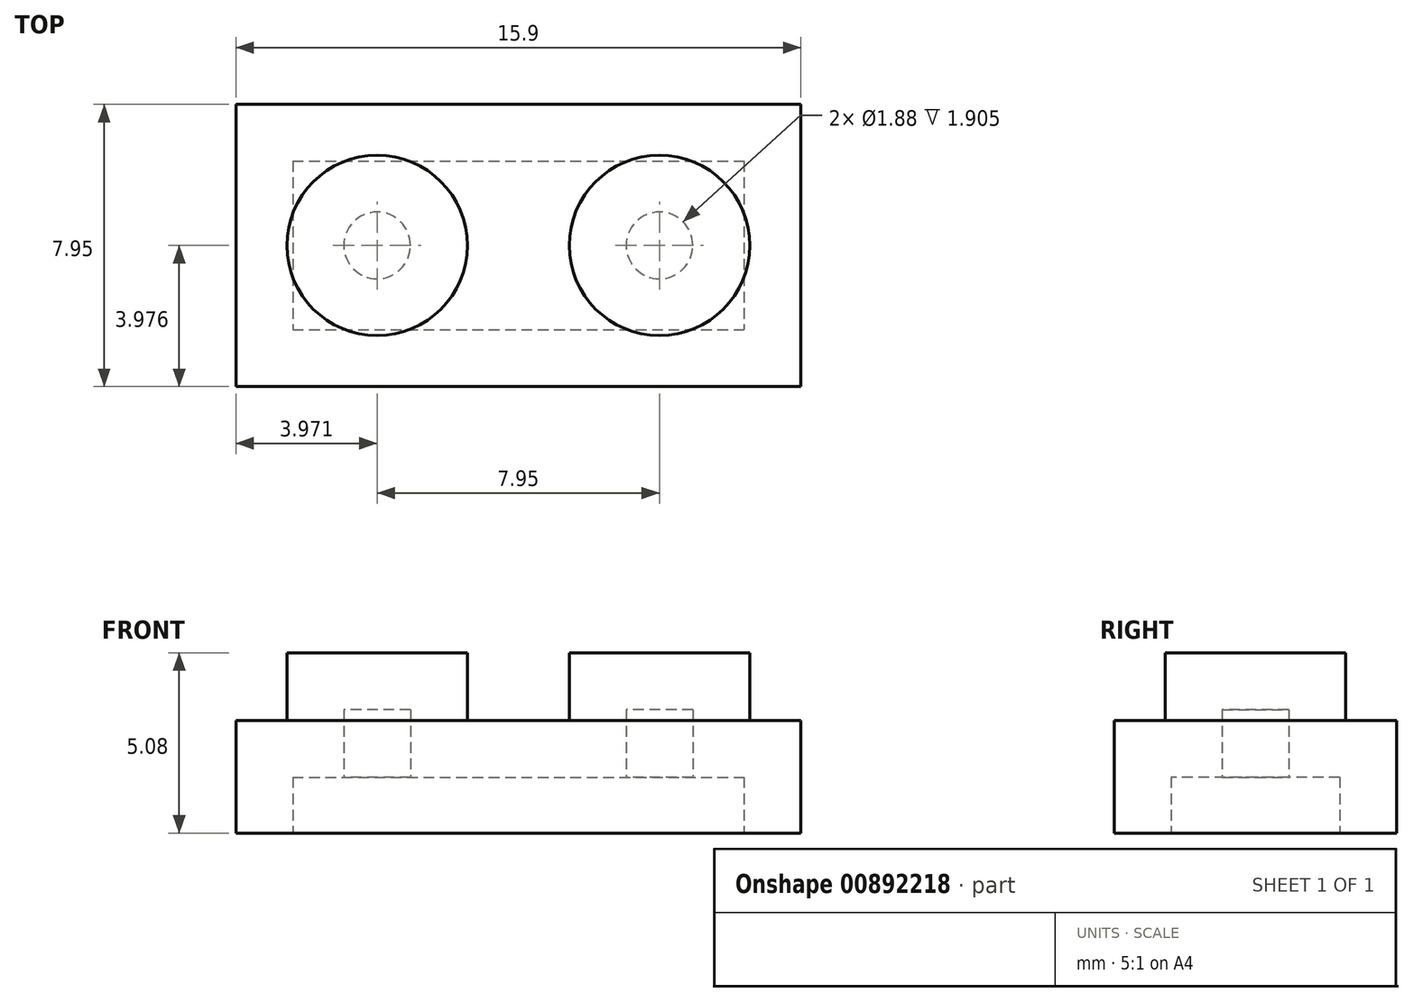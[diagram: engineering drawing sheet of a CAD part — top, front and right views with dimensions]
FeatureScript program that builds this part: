
annotation { "Feature Type Name" : "Feature", "Feature Type Description" : "" }
export const myFeature = defineFeature(function(context is Context, id is Id, definition is map)
    precondition{}
    {
        {
            var Q0;
            Q0=qCreatedBy(makeId("Top.planeOp"),FACE);
            var sketch = newSketch(context, id + "F0", { "sketchPlane" : qUnion([Q0])});
            skLineSegment(sketch, "E0.bottom", {"start": v(-57.35, -17.93) * mm, "end": v(-41.45, -17.93) * mm});
            skLineSegment(sketch, "E0.top", {"start": v(-57.35, -25.88) * mm, "end": v(-41.45, -25.88) * mm});
            skLineSegment(sketch, "E0.left", {"start": v(-57.35, -17.93) * mm, "end": v(-57.35, -25.88) * mm});
            skLineSegment(sketch, "E0.right", {"start": v(-41.45, -17.93) * mm, "end": v(-41.45, -25.88) * mm});
            skLineSegment(sketch, "E1", {"start": v(-53.38, -17.93) * mm, "end": v(-53.38, -25.88) * mm});
            skLineSegment(sketch, "E2", {"start": v(-45.43, -17.93) * mm, "end": v(-45.43, -25.88) * mm});
            skCircle(sketch, "E3", {"center": v(-53.38, -21.9) * mm, "radius": 2.54 * mm});
            skCircle(sketch, "E4", {"center": v(-45.43, -21.9) * mm, "radius": 2.54 * mm});
            skSolve(sketch);
        }
        {
            var Q0;
            {var subQ0=sQuery(id+"F0.wireOp",EDGE,"E0.left");Q0=makeQuery(id+"F0.imprint","IMPRINT",FACE,{"disambiguationData":[TD([[makeQuery(id+"F0.imprint","IMPRINT",EDGE,{"derivedFrom":subQ0}),1.0]])]});}
            var Q1;
            {var subQ0=sQuery(id+"F0.wireOp",EDGE,"E1");var subQ5=sQuery(id+"F0.wireOp",EDGE,"E0.bottom");var subQ6=makeQuery(id+"F0.imprint","INTERSECT",VERTEX,{"derivedFrom":[subQ5,subQ0]});Q1=makeQuery(id+"F0.imprint","IMPRINT",FACE,{"disambiguationData":[TD([[makeQuery(id+"F0.imprint","IMPRINT",EDGE,{"disambiguationData":[TD([[subQ6,-1.0]])],"derivedFrom":subQ5}),-1.0]])]});}
            var Q2;
            {var subQ5=sQuery(id+"F0.wireOp",EDGE,"E0.right");Q2=makeQuery(id+"F0.imprint","IMPRINT",FACE,{"disambiguationData":[TD([[makeQuery(id+"F0.imprint","IMPRINT",EDGE,{"derivedFrom":subQ5}),-1.0]])]});}
            var Q3;
            {var subQ0=sQuery(id+"F0.wireOp",EDGE,"E4");var subQ1=sQuery(id+"F0.wireOp",EDGE,"E2");var subQ2=makeQuery(id+"F0.imprint","INTERSECT",VERTEX,{"disambiguationData":[OD(0.0)],"derivedFrom":[subQ1,subQ0]});Q3=makeQuery(id+"F0.imprint","IMPRINT",FACE,{"disambiguationData":[TD([[makeQuery(id+"F0.imprint","IMPRINT",EDGE,{"disambiguationData":[TD([[subQ2,-1.0]])],"derivedFrom":subQ1}),-1.0]])]});}
            var Q4;
            {var subQ0=sQuery(id+"F0.wireOp",EDGE,"E4");var subQ1=sQuery(id+"F0.wireOp",EDGE,"E2");var subQ2=makeQuery(id+"F0.imprint","INTERSECT",VERTEX,{"disambiguationData":[OD(0.0)],"derivedFrom":[subQ1,subQ0]});Q4=makeQuery(id+"F0.imprint","IMPRINT",FACE,{"disambiguationData":[TD([[makeQuery(id+"F0.imprint","IMPRINT",EDGE,{"disambiguationData":[TD([[subQ2,-1.0]])],"derivedFrom":subQ1}),1.0]])]});}
            var Q5;
            {var subQ0=sQuery(id+"F0.wireOp",EDGE,"E3");var subQ1=sQuery(id+"F0.wireOp",EDGE,"E1");var subQ2=makeQuery(id+"F0.imprint","INTERSECT",VERTEX,{"disambiguationData":[OD(0.0)],"derivedFrom":[subQ1,subQ0]});Q5=makeQuery(id+"F0.imprint","IMPRINT",FACE,{"disambiguationData":[TD([[makeQuery(id+"F0.imprint","IMPRINT",EDGE,{"disambiguationData":[TD([[subQ2,-1.0]])],"derivedFrom":subQ1}),1.0]])]});}
            var Q6;
            {var subQ0=sQuery(id+"F0.wireOp",EDGE,"E3");var subQ1=sQuery(id+"F0.wireOp",EDGE,"E1");var subQ2=makeQuery(id+"F0.imprint","INTERSECT",VERTEX,{"disambiguationData":[OD(0.0)],"derivedFrom":[subQ1,subQ0]});Q6=makeQuery(id+"F0.imprint","IMPRINT",FACE,{"disambiguationData":[TD([[makeQuery(id+"F0.imprint","IMPRINT",EDGE,{"disambiguationData":[TD([[subQ2,-1.0]])],"derivedFrom":subQ1}),-1.0]])]});}
            extrude(context, id + "F1", {"entities" : qUnion([Q0, Q1, Q2, Q3, Q4, Q5, Q6]), "depth" : 3.17 * mm, "offsetDistance" : 25.4 * mm});
        }
        {
            var Q0;
            {var subQ0=sQuery(id+"F0.wireOp",EDGE,"E3");var subQ1=sQuery(id+"F0.wireOp",EDGE,"E1");var subQ2=makeQuery(id+"F0.imprint","INTERSECT",VERTEX,{"disambiguationData":[OD(0.0)],"derivedFrom":[subQ1,subQ0]});Q0=makeQuery(id+"F0.imprint","IMPRINT",FACE,{"disambiguationData":[TD([[makeQuery(id+"F0.imprint","IMPRINT",EDGE,{"disambiguationData":[TD([[subQ2,-1.0]])],"derivedFrom":subQ1}),-1.0]])]});}
            var Q1;
            {var subQ0=sQuery(id+"F0.wireOp",EDGE,"E3");var subQ1=sQuery(id+"F0.wireOp",EDGE,"E1");var subQ2=makeQuery(id+"F0.imprint","INTERSECT",VERTEX,{"disambiguationData":[OD(0.0)],"derivedFrom":[subQ1,subQ0]});Q1=makeQuery(id+"F0.imprint","IMPRINT",FACE,{"disambiguationData":[TD([[makeQuery(id+"F0.imprint","IMPRINT",EDGE,{"disambiguationData":[TD([[subQ2,-1.0]])],"derivedFrom":subQ1}),1.0]])]});}
            var Q2;
            {var subQ0=sQuery(id+"F0.wireOp",EDGE,"E4");var subQ1=sQuery(id+"F0.wireOp",EDGE,"E2");var subQ2=makeQuery(id+"F0.imprint","INTERSECT",VERTEX,{"disambiguationData":[OD(0.0)],"derivedFrom":[subQ1,subQ0]});Q2=makeQuery(id+"F0.imprint","IMPRINT",FACE,{"disambiguationData":[TD([[makeQuery(id+"F0.imprint","IMPRINT",EDGE,{"disambiguationData":[TD([[subQ2,-1.0]])],"derivedFrom":subQ1}),-1.0]])]});}
            var Q3;
            {var subQ0=sQuery(id+"F0.wireOp",EDGE,"E4");var subQ1=sQuery(id+"F0.wireOp",EDGE,"E2");var subQ2=makeQuery(id+"F0.imprint","INTERSECT",VERTEX,{"disambiguationData":[OD(0.0)],"derivedFrom":[subQ1,subQ0]});Q3=makeQuery(id+"F0.imprint","IMPRINT",FACE,{"disambiguationData":[TD([[makeQuery(id+"F0.imprint","IMPRINT",EDGE,{"disambiguationData":[TD([[subQ2,-1.0]])],"derivedFrom":subQ1}),1.0]])]});}
            extrude(context, id + "F2", {"entities" : qUnion([Q0, Q1, Q2, Q3]), "operationType" : NewBodyOperationType.ADD, "depth" : 5.08 * mm, "offsetDistance" : 25.4 * mm});
        }
        {
            var Q0;
            Q0=makeQuery(id+"F1.opExtrude","CAP_FACE",FACE,{"disambiguationData":[OSD([sQuery(id+"F0.wireOp",EDGE,"E0.bottom"),sQuery(id+"F0.wireOp",EDGE,"E0.top"),sQuery(id+"F0.wireOp",EDGE,"E0.left"),sQuery(id+"F0.wireOp",EDGE,"E0.right")])],"isStart":true});
            shell(context, id + "F3", {"entities" : qUnion([Q0]), "thickness" : 1.6 * mm});
        }
    });
